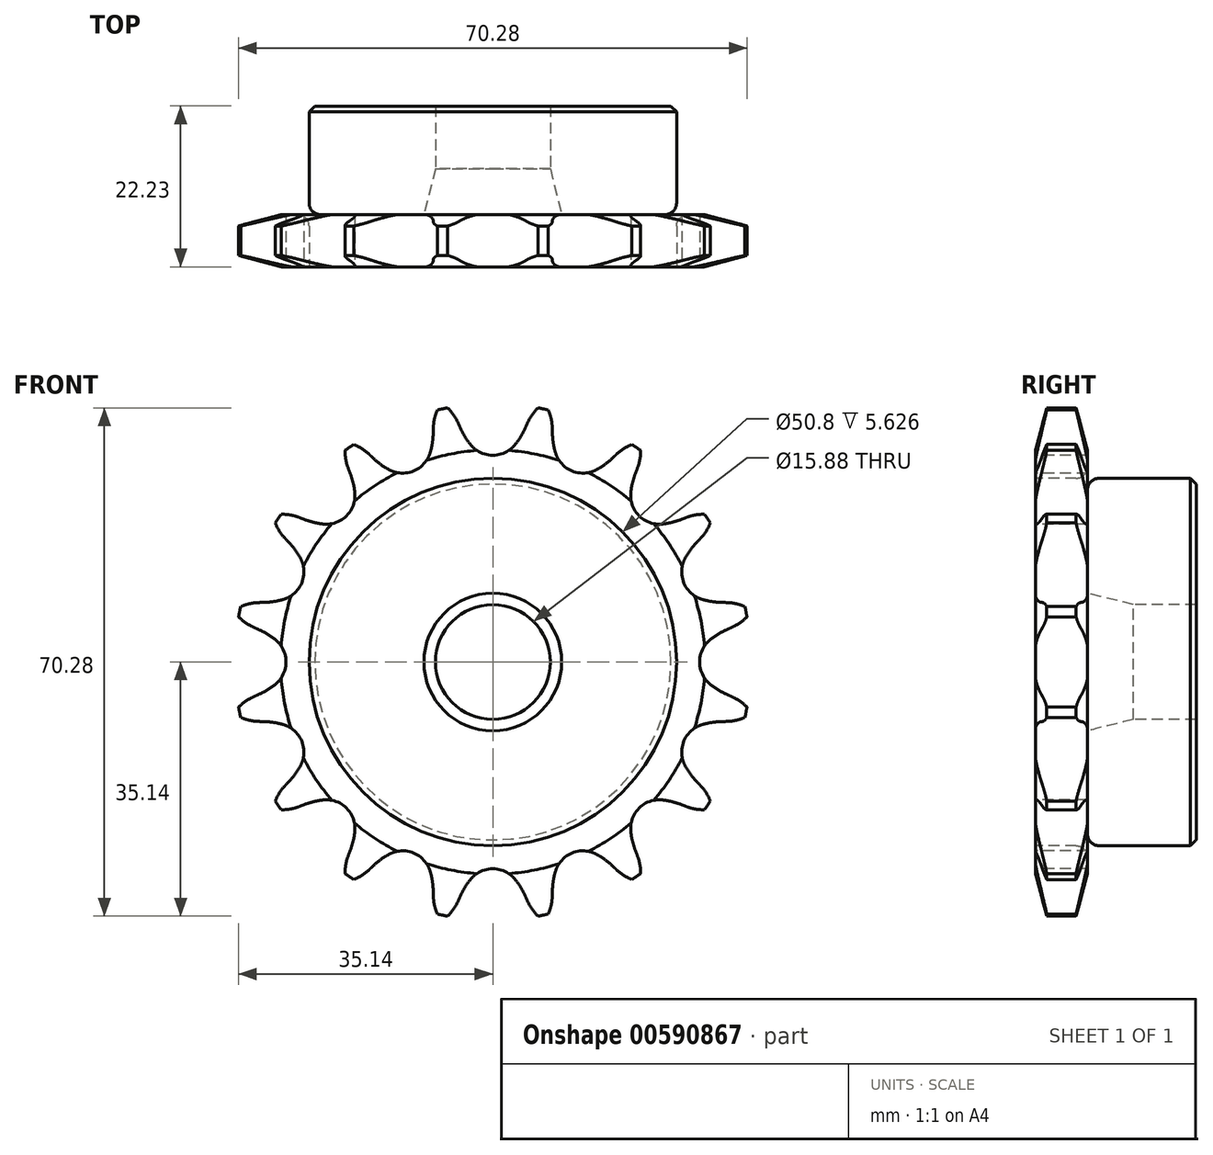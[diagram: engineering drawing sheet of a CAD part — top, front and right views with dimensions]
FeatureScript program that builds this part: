
annotation { "Feature Type Name" : "Feature", "Feature Type Description" : "" }
export const myFeature = defineFeature(function(context is Context, id is Id, definition is map)
    precondition{}
    {
        {
            var Q0;
            Q0=qCreatedBy(makeId("Right.planeOp"),FACE);
            var sketch = newSketch(context, id + "F0", { "sketchPlane" : qUnion([Q0])});
            skLineSegment(sketch, "E0", {"start": v(0, 0) * mm, "end": v(22.23, 0) * mm, "construction": true});
            skLineSegment(sketch, "E1.bottom", {"start": v(0, 7.94) * mm, "end": v(7.21, 7.94) * mm});
            skLineSegment(sketch, "E1.top", {"start": v(0, 35.69) * mm, "end": v(7.21, 35.69) * mm});
            skLineSegment(sketch, "E1.left", {"start": v(0, 7.94) * mm, "end": v(0, 35.69) * mm});
            skLineSegment(sketch, "E1.right", {"start": v(7.21, 7.94) * mm, "end": v(7.21, 35.69) * mm});
            skLineSegment(sketch, "E2.bottom", {"start": v(0, 7.94) * mm, "end": v(22.23, 7.94) * mm});
            skLineSegment(sketch, "E2.top", {"start": v(0, 25.4) * mm, "end": v(22.23, 25.4) * mm});
            skLineSegment(sketch, "E2.left", {"start": v(0, 7.94) * mm, "end": v(0, 25.4) * mm});
            skLineSegment(sketch, "E2.right", {"start": v(22.23, 7.94) * mm, "end": v(22.22, 25.4) * mm});
            skLineSegment(sketch, "E3.MirrorCS", {"start": v(0, -7.94) * mm, "end": v(7.21, -7.94) * mm});
            skLineSegment(sketch, "E4.MirrorCS", {"start": v(22.23, -7.94) * mm, "end": v(22.23, -25.4) * mm});
            skLineSegment(sketch, "E5.MirrorCS", {"start": v(0, -7.94) * mm, "end": v(0, -25.4) * mm});
            skLineSegment(sketch, "E6.MirrorCS", {"start": v(0, -35.69) * mm, "end": v(7.21, -35.69) * mm});
            skLineSegment(sketch, "E7.MirrorCS", {"start": v(0, -25.4) * mm, "end": v(22.23, -25.4) * mm});
            skLineSegment(sketch, "E8.MirrorCS", {"start": v(0, -7.94) * mm, "end": v(22.23, -7.94) * mm});
            skLineSegment(sketch, "E9.MirrorCS", {"start": v(0, -7.94) * mm, "end": v(0, -35.69) * mm});
            skLineSegment(sketch, "E10.MirrorCS", {"start": v(7.21, -7.94) * mm, "end": v(7.21, -35.69) * mm});
            skSolve(sketch);
        }
        {
            var Q0;
            {var subQ5=sQuery(id+"F0.wireOp",EDGE,"E2.right");Q0=makeQuery(id+"F0.imprint","IMPRINT",FACE,{"disambiguationData":[TD([[makeQuery(id+"F0.imprint","IMPRINT",EDGE,{"derivedFrom":subQ5}),1.0]])]});}
            var Q1;
            {var subQ5=sQuery(id+"F0.wireOp",EDGE,"E2.left");Q1=makeQuery(id+"F0.imprint","IMPRINT",FACE,{"disambiguationData":[TD([[makeQuery(id+"F0.imprint","IMPRINT",EDGE,{"derivedFrom":subQ5}),-1.0]])]});}
            var Q2;
            {var subQ0=sQuery(id+"F0.wireOp",EDGE,"E1.top");Q2=makeQuery(id+"F0.imprint","IMPRINT",FACE,{"disambiguationData":[TD([[makeQuery(id+"F0.imprint","IMPRINT",EDGE,{"derivedFrom":subQ0}),-1.0]])]});}
            var Q3;
            Q3=sQuery(id+"F0.wireOp",EDGE,"E0");
            revolve(context, id + "F1", {"entities" : qUnion([Q0, Q1, Q2]), "axis" : qUnion([Q3]), "revolveType" : RevolveType.FULL});
        }
        {
            var Q0;
            Q0=makeQuery(id+"F1.opRevolve","SWEPT_EDGE",EDGE,{"disambiguationData":[OSD([sQuery(id+"F0.wireOp",EDGE,"E1.right"),sQuery(id+"F0.wireOp",EDGE,"E2.top")])]});
            fillet(context, id + "F2", {"entities" : qUnion([Q0]), "radius" : 1.59 * mm, "tangentPropagation" : true, "allowEdgeOverflow" : false});
        }
        {
            var Q0;
            Q0=makeQuery(id+"F1.opRevolve","SWEPT_EDGE",EDGE,{"disambiguationData":[OSD([sQuery(id+"F0.wireOp",EDGE,"E2.top"),sQuery(id+"F0.wireOp",EDGE,"E2.right")])]});
            chamfer(context, id + "F3", {"entities" : qUnion([Q0]), "width" : 0.8 * mm, "tangentPropagation" : true});
        }
        {
            var Q0;
            Q0=makeQuery(id+"F1.opRevolve","SWEPT_EDGE",EDGE,{"disambiguationData":[OSD([sQuery(id+"F0.wireOp",EDGE,"E1.top"),sQuery(id+"F0.wireOp",EDGE,"E1.left")])]});
            var Q1;
            Q1=makeQuery(id+"F1.opRevolve","SWEPT_FACE",FACE,{"disambiguationData":[OSD([sQuery(id+"F0.wireOp",EDGE,"E1.right")])]});
            chamfer(context, id + "F4", {"entities" : qUnion([Q0, Q1]), "chamferType" : ChamferType.TWO_OFFSETS, "width1" : 6.35 * mm, "oppositeDirection" : false, "width2" : 1.57 * mm, "tangentPropagation" : true});
        }
        {
            var Q0;
            Q0=makeQuery(id+"F1.opRevolve","SWEPT_FACE",FACE,{"disambiguationData":[OSD([sQuery(id+"F0.wireOp",EDGE,"E1.left"),sQuery(id+"F0.wireOp",EDGE,"E2.left")])]});
            var sketch = newSketch(context, id + "F5", { "sketchPlane" : qUnion([Q0])});
            skCircle(sketch, "E11", {"center": v(0, 0) * mm, "radius": 32.55 * mm, "construction": true});
            skLineSegment(sketch, "E12", {"start": v(0, 0) * mm, "end": v(0, 32.55) * mm, "construction": true});
            skLineSegment(sketch, "E13", {"start": v(0, 32.55) * mm, "end": v(34.9, 32.55) * mm, "construction": true});
            skLineSegment(sketch, "E14", {"start": v(0, 32.55) * mm, "end": v(5, 36.56) * mm, "construction": true});
            skLineSegment(sketch, "E15", {"start": v(5, 36.56) * mm, "end": v(-4.46, 32.3) * mm, "construction": true});
            skLineSegment(sketch, "E16", {"start": v(-4.46, 32.3) * mm, "end": v(-4.82, 33.1) * mm});
            skLineSegment(sketch, "E17", {"start": v(0, 0) * mm, "end": v(-7.13, 35.85) * mm, "construction": true});
            skArc(sketch, "E18", {"start": v(-7.13, 35.85) * mm, "mid": v(-15.87, 26.15) * mm, "end": v(-4.82, 33.1) * mm, "construction": true});
            skLineSegment(sketch, "E19", {"start": v(-4.82, 33.1) * mm, "end": v(-4.82, 33.1) * mm});
            skArc(sketch, "E20", {"start": v(-4.82, 33.1) * mm, "mid": v(-5.78, 34.63) * mm, "end": v(-7.13, 35.85) * mm});
            skLineSegment(sketch, "E21", {"start": v(-4.46, 32.3) * mm, "end": v(-4.46, 32.3) * mm});
            skArc(sketch, "E22", {"start": v(-3.1, 30.07) * mm, "mid": v(13.83, 41.97) * mm, "end": v(-4.46, 32.3) * mm, "construction": true});
            skLineSegment(sketch, "E23", {"start": v(-4.82, 33.1) * mm, "end": v(-4.46, 32.3) * mm});
            skArc(sketch, "E24", {"start": v(-4.46, 32.3) * mm, "mid": v(-3.84, 31.14) * mm, "end": v(-3.1, 30.07) * mm});
            skArc(sketch, "E25.MirrorCS", {"start": v(4.82, 33.1) * mm, "mid": v(5.78, 34.63) * mm, "end": v(7.13, 35.85) * mm});
            skLineSegment(sketch, "E26.MirrorCS", {"start": v(4.82, 33.1) * mm, "end": v(4.46, 32.3) * mm});
            skArc(sketch, "E27.MirrorCS", {"start": v(4.46, 32.3) * mm, "mid": v(3.84, 31.14) * mm, "end": v(3.1, 30.07) * mm});
            skArc(sketch, "E28", {"start": v(3.1, 30.07) * mm, "mid": v(0, 36.51) * mm, "end": v(-3.1, 30.07) * mm, "construction": true});
            skArc(sketch, "E29", {"start": v(-3.1, 30.07) * mm, "mid": v(0, 28.59) * mm, "end": v(3.1, 30.07) * mm});
            skArc(sketch, "E30.1.0", {"start": v(-17.12, 28.74) * mm, "mid": v(-18.6, 29.79) * mm, "end": v(-20.3, 30.4) * mm});
            skLineSegment(sketch, "E30.1.1", {"start": v(-17.12, 28.74) * mm, "end": v(-16.48, 28.14) * mm});
            skArc(sketch, "E30.1.2", {"start": v(-16.48, 28.14) * mm, "mid": v(-15.47, 27.3) * mm, "end": v(-14.36, 26.6) * mm});
            skArc(sketch, "E30.1.3", {"start": v(-14.36, 26.6) * mm, "mid": v(-10.94, 26.41) * mm, "end": v(-8.65, 28.96) * mm});
            skArc(sketch, "E30.1.4", {"start": v(-8.24, 31.55) * mm, "mid": v(-8.37, 30.24) * mm, "end": v(-8.65, 28.96) * mm});
            skLineSegment(sketch, "E30.1.5", {"start": v(-8.22, 32.42) * mm, "end": v(-8.24, 31.55) * mm});
            skArc(sketch, "E30.1.6", {"start": v(-8.22, 32.42) * mm, "mid": v(-7.91, 34.21) * mm, "end": v(-7.13, 35.85) * mm});
            skArc(sketch, "E30.2.0", {"start": v(-26.8, 20) * mm, "mid": v(-28.58, 20.4) * mm, "end": v(-30.4, 20.3) * mm});
            skLineSegment(sketch, "E30.2.1", {"start": v(-26.8, 20) * mm, "end": v(-26, 19.69) * mm});
            skArc(sketch, "E30.2.2", {"start": v(-26, 19.69) * mm, "mid": v(-24.74, 19.3) * mm, "end": v(-23.45, 19.08) * mm});
            skArc(sketch, "E30.2.3", {"start": v(-23.45, 19.08) * mm, "mid": v(-20.21, 20.21) * mm, "end": v(-19.08, 23.45) * mm});
            skArc(sketch, "E30.2.4", {"start": v(-19.69, 26) * mm, "mid": v(-19.3, 24.74) * mm, "end": v(-19.08, 23.45) * mm});
            skLineSegment(sketch, "E30.2.5", {"start": v(-20, 26.8) * mm, "end": v(-19.69, 26) * mm});
            skArc(sketch, "E30.2.6", {"start": v(-20, 26.8) * mm, "mid": v(-20.4, 28.58) * mm, "end": v(-20.3, 30.4) * mm});
            skArc(sketch, "E30.3.0", {"start": v(-32.42, 8.22) * mm, "mid": v(-34.21, 7.91) * mm, "end": v(-35.85, 7.13) * mm});
            skLineSegment(sketch, "E30.3.1", {"start": v(-32.42, 8.22) * mm, "end": v(-31.55, 8.24) * mm});
            skArc(sketch, "E30.3.2", {"start": v(-31.55, 8.24) * mm, "mid": v(-30.24, 8.37) * mm, "end": v(-28.96, 8.65) * mm});
            skArc(sketch, "E30.3.3", {"start": v(-28.96, 8.65) * mm, "mid": v(-26.41, 10.94) * mm, "end": v(-26.6, 14.36) * mm});
            skArc(sketch, "E30.3.4", {"start": v(-28.14, 16.48) * mm, "mid": v(-27.3, 15.47) * mm, "end": v(-26.6, 14.36) * mm});
            skLineSegment(sketch, "E30.3.5", {"start": v(-28.74, 17.12) * mm, "end": v(-28.14, 16.48) * mm});
            skArc(sketch, "E30.3.6", {"start": v(-28.74, 17.12) * mm, "mid": v(-29.79, 18.6) * mm, "end": v(-30.4, 20.3) * mm});
            skArc(sketch, "E30.4.0", {"start": v(-33.1, -4.82) * mm, "mid": v(-34.63, -5.78) * mm, "end": v(-35.85, -7.13) * mm});
            skLineSegment(sketch, "E30.4.1", {"start": v(-33.1, -4.82) * mm, "end": v(-32.3, -4.46) * mm});
            skArc(sketch, "E30.4.2", {"start": v(-32.3, -4.46) * mm, "mid": v(-31.14, -3.84) * mm, "end": v(-30.07, -3.1) * mm});
            skArc(sketch, "E30.4.3", {"start": v(-30.07, -3.1) * mm, "mid": v(-28.59, 0) * mm, "end": v(-30.07, 3.1) * mm});
            skArc(sketch, "E30.4.4", {"start": v(-32.3, 4.46) * mm, "mid": v(-31.14, 3.84) * mm, "end": v(-30.07, 3.1) * mm});
            skLineSegment(sketch, "E30.4.5", {"start": v(-33.1, 4.82) * mm, "end": v(-32.3, 4.46) * mm});
            skArc(sketch, "E30.4.6", {"start": v(-33.1, 4.82) * mm, "mid": v(-34.63, 5.78) * mm, "end": v(-35.85, 7.13) * mm});
            skArc(sketch, "E30.5.0", {"start": v(-28.74, -17.12) * mm, "mid": v(-29.79, -18.6) * mm, "end": v(-30.4, -20.3) * mm});
            skLineSegment(sketch, "E30.5.1", {"start": v(-28.74, -17.12) * mm, "end": v(-28.14, -16.48) * mm});
            skArc(sketch, "E30.5.2", {"start": v(-28.14, -16.48) * mm, "mid": v(-27.3, -15.47) * mm, "end": v(-26.6, -14.36) * mm});
            skArc(sketch, "E30.5.3", {"start": v(-26.6, -14.36) * mm, "mid": v(-26.41, -10.94) * mm, "end": v(-28.96, -8.65) * mm});
            skArc(sketch, "E30.5.4", {"start": v(-31.55, -8.24) * mm, "mid": v(-30.24, -8.37) * mm, "end": v(-28.96, -8.65) * mm});
            skLineSegment(sketch, "E30.5.5", {"start": v(-32.42, -8.22) * mm, "end": v(-31.55, -8.24) * mm});
            skArc(sketch, "E30.5.6", {"start": v(-32.42, -8.22) * mm, "mid": v(-34.21, -7.91) * mm, "end": v(-35.85, -7.13) * mm});
            skArc(sketch, "E30.6.0", {"start": v(-20, -26.8) * mm, "mid": v(-20.4, -28.58) * mm, "end": v(-20.3, -30.4) * mm});
            skLineSegment(sketch, "E30.6.1", {"start": v(-20, -26.8) * mm, "end": v(-19.69, -26) * mm});
            skArc(sketch, "E30.6.2", {"start": v(-19.69, -26) * mm, "mid": v(-19.3, -24.74) * mm, "end": v(-19.08, -23.45) * mm});
            skArc(sketch, "E30.6.3", {"start": v(-19.08, -23.45) * mm, "mid": v(-20.21, -20.21) * mm, "end": v(-23.45, -19.08) * mm});
            skArc(sketch, "E30.6.4", {"start": v(-26, -19.69) * mm, "mid": v(-24.74, -19.3) * mm, "end": v(-23.45, -19.08) * mm});
            skLineSegment(sketch, "E30.6.5", {"start": v(-26.8, -20) * mm, "end": v(-26, -19.69) * mm});
            skArc(sketch, "E30.6.6", {"start": v(-26.8, -20) * mm, "mid": v(-28.58, -20.4) * mm, "end": v(-30.4, -20.3) * mm});
            skArc(sketch, "E30.7.0", {"start": v(-8.22, -32.42) * mm, "mid": v(-7.91, -34.21) * mm, "end": v(-7.13, -35.85) * mm});
            skLineSegment(sketch, "E30.7.1", {"start": v(-8.22, -32.42) * mm, "end": v(-8.24, -31.55) * mm});
            skArc(sketch, "E30.7.2", {"start": v(-8.24, -31.55) * mm, "mid": v(-8.37, -30.24) * mm, "end": v(-8.65, -28.96) * mm});
            skArc(sketch, "E30.7.3", {"start": v(-8.65, -28.96) * mm, "mid": v(-10.94, -26.41) * mm, "end": v(-14.36, -26.6) * mm});
            skArc(sketch, "E30.7.4", {"start": v(-16.48, -28.14) * mm, "mid": v(-15.47, -27.3) * mm, "end": v(-14.36, -26.6) * mm});
            skLineSegment(sketch, "E30.7.5", {"start": v(-17.12, -28.74) * mm, "end": v(-16.48, -28.14) * mm});
            skArc(sketch, "E30.7.6", {"start": v(-17.12, -28.74) * mm, "mid": v(-18.6, -29.79) * mm, "end": v(-20.3, -30.4) * mm});
            skArc(sketch, "E30.8.0", {"start": v(4.82, -33.1) * mm, "mid": v(5.78, -34.63) * mm, "end": v(7.13, -35.85) * mm});
            skLineSegment(sketch, "E30.8.1", {"start": v(4.82, -33.1) * mm, "end": v(4.46, -32.3) * mm});
            skArc(sketch, "E30.8.2", {"start": v(4.46, -32.3) * mm, "mid": v(3.84, -31.14) * mm, "end": v(3.1, -30.07) * mm});
            skArc(sketch, "E30.8.3", {"start": v(3.1, -30.07) * mm, "mid": v(0, -28.59) * mm, "end": v(-3.1, -30.07) * mm});
            skArc(sketch, "E30.8.4", {"start": v(-4.46, -32.3) * mm, "mid": v(-3.84, -31.14) * mm, "end": v(-3.1, -30.07) * mm});
            skLineSegment(sketch, "E30.8.5", {"start": v(-4.82, -33.1) * mm, "end": v(-4.46, -32.3) * mm});
            skArc(sketch, "E30.8.6", {"start": v(-4.82, -33.1) * mm, "mid": v(-5.78, -34.63) * mm, "end": v(-7.13, -35.85) * mm});
            skArc(sketch, "E30.9.0", {"start": v(17.12, -28.74) * mm, "mid": v(18.6, -29.79) * mm, "end": v(20.3, -30.4) * mm});
            skLineSegment(sketch, "E30.9.1", {"start": v(17.12, -28.74) * mm, "end": v(16.48, -28.14) * mm});
            skArc(sketch, "E30.9.2", {"start": v(16.48, -28.14) * mm, "mid": v(15.47, -27.3) * mm, "end": v(14.36, -26.6) * mm});
            skArc(sketch, "E30.9.3", {"start": v(14.36, -26.6) * mm, "mid": v(10.94, -26.41) * mm, "end": v(8.65, -28.96) * mm});
            skArc(sketch, "E30.9.4", {"start": v(8.24, -31.55) * mm, "mid": v(8.37, -30.24) * mm, "end": v(8.65, -28.96) * mm});
            skLineSegment(sketch, "E30.9.5", {"start": v(8.22, -32.42) * mm, "end": v(8.24, -31.55) * mm});
            skArc(sketch, "E30.9.6", {"start": v(8.22, -32.42) * mm, "mid": v(7.91, -34.21) * mm, "end": v(7.13, -35.85) * mm});
            skArc(sketch, "E30.10.0", {"start": v(26.8, -20) * mm, "mid": v(28.58, -20.4) * mm, "end": v(30.4, -20.3) * mm});
            skLineSegment(sketch, "E30.10.1", {"start": v(26.8, -20) * mm, "end": v(26, -19.69) * mm});
            skArc(sketch, "E30.10.2", {"start": v(26, -19.69) * mm, "mid": v(24.74, -19.3) * mm, "end": v(23.45, -19.08) * mm});
            skArc(sketch, "E30.10.3", {"start": v(23.45, -19.08) * mm, "mid": v(20.21, -20.21) * mm, "end": v(19.08, -23.45) * mm});
            skArc(sketch, "E30.10.4", {"start": v(19.69, -26) * mm, "mid": v(19.3, -24.74) * mm, "end": v(19.08, -23.45) * mm});
            skLineSegment(sketch, "E30.10.5", {"start": v(20, -26.8) * mm, "end": v(19.69, -26) * mm});
            skArc(sketch, "E30.10.6", {"start": v(20, -26.8) * mm, "mid": v(20.4, -28.58) * mm, "end": v(20.3, -30.4) * mm});
            skArc(sketch, "E30.11.0", {"start": v(32.42, -8.22) * mm, "mid": v(34.21, -7.91) * mm, "end": v(35.85, -7.13) * mm});
            skLineSegment(sketch, "E30.11.1", {"start": v(32.42, -8.22) * mm, "end": v(31.55, -8.24) * mm});
            skArc(sketch, "E30.11.2", {"start": v(31.55, -8.24) * mm, "mid": v(30.24, -8.37) * mm, "end": v(28.96, -8.65) * mm});
            skArc(sketch, "E30.11.3", {"start": v(28.96, -8.65) * mm, "mid": v(26.41, -10.94) * mm, "end": v(26.6, -14.36) * mm});
            skArc(sketch, "E30.11.4", {"start": v(28.14, -16.48) * mm, "mid": v(27.3, -15.47) * mm, "end": v(26.6, -14.36) * mm});
            skLineSegment(sketch, "E30.11.5", {"start": v(28.74, -17.12) * mm, "end": v(28.14, -16.48) * mm});
            skArc(sketch, "E30.11.6", {"start": v(28.74, -17.12) * mm, "mid": v(29.79, -18.6) * mm, "end": v(30.4, -20.3) * mm});
            skArc(sketch, "E30.12.0", {"start": v(33.1, 4.82) * mm, "mid": v(34.63, 5.78) * mm, "end": v(35.85, 7.13) * mm});
            skLineSegment(sketch, "E30.12.1", {"start": v(33.1, 4.82) * mm, "end": v(32.3, 4.46) * mm});
            skArc(sketch, "E30.12.2", {"start": v(32.3, 4.46) * mm, "mid": v(31.14, 3.84) * mm, "end": v(30.07, 3.1) * mm});
            skArc(sketch, "E30.12.3", {"start": v(30.07, 3.1) * mm, "mid": v(28.59, 0) * mm, "end": v(30.07, -3.1) * mm});
            skArc(sketch, "E30.12.4", {"start": v(32.3, -4.46) * mm, "mid": v(31.14, -3.84) * mm, "end": v(30.07, -3.1) * mm});
            skLineSegment(sketch, "E30.12.5", {"start": v(33.1, -4.82) * mm, "end": v(32.3, -4.46) * mm});
            skArc(sketch, "E30.12.6", {"start": v(33.1, -4.82) * mm, "mid": v(34.63, -5.78) * mm, "end": v(35.85, -7.13) * mm});
            skArc(sketch, "E30.13.0", {"start": v(28.74, 17.12) * mm, "mid": v(29.79, 18.6) * mm, "end": v(30.4, 20.3) * mm});
            skLineSegment(sketch, "E30.13.1", {"start": v(28.74, 17.12) * mm, "end": v(28.14, 16.48) * mm});
            skArc(sketch, "E30.13.2", {"start": v(28.14, 16.48) * mm, "mid": v(27.3, 15.47) * mm, "end": v(26.6, 14.36) * mm});
            skArc(sketch, "E30.13.3", {"start": v(26.6, 14.36) * mm, "mid": v(26.41, 10.94) * mm, "end": v(28.96, 8.65) * mm});
            skArc(sketch, "E30.13.4", {"start": v(31.55, 8.24) * mm, "mid": v(30.24, 8.37) * mm, "end": v(28.96, 8.65) * mm});
            skLineSegment(sketch, "E30.13.5", {"start": v(32.42, 8.22) * mm, "end": v(31.55, 8.24) * mm});
            skArc(sketch, "E30.13.6", {"start": v(32.42, 8.22) * mm, "mid": v(34.21, 7.91) * mm, "end": v(35.85, 7.13) * mm});
            skArc(sketch, "E30.14.0", {"start": v(20, 26.8) * mm, "mid": v(20.4, 28.58) * mm, "end": v(20.3, 30.4) * mm});
            skLineSegment(sketch, "E30.14.1", {"start": v(20, 26.8) * mm, "end": v(19.69, 26) * mm});
            skArc(sketch, "E30.14.2", {"start": v(19.69, 26) * mm, "mid": v(19.3, 24.74) * mm, "end": v(19.08, 23.45) * mm});
            skArc(sketch, "E30.14.3", {"start": v(19.08, 23.45) * mm, "mid": v(20.21, 20.21) * mm, "end": v(23.45, 19.08) * mm});
            skArc(sketch, "E30.14.4", {"start": v(26, 19.69) * mm, "mid": v(24.74, 19.3) * mm, "end": v(23.45, 19.08) * mm});
            skLineSegment(sketch, "E30.14.5", {"start": v(26.8, 20) * mm, "end": v(26, 19.69) * mm});
            skArc(sketch, "E30.14.6", {"start": v(26.8, 20) * mm, "mid": v(28.58, 20.4) * mm, "end": v(30.4, 20.3) * mm});
            skArc(sketch, "E30.15.0", {"start": v(8.22, 32.42) * mm, "mid": v(7.91, 34.21) * mm, "end": v(7.13, 35.85) * mm});
            skLineSegment(sketch, "E30.15.1", {"start": v(8.22, 32.42) * mm, "end": v(8.24, 31.55) * mm});
            skArc(sketch, "E30.15.2", {"start": v(8.24, 31.55) * mm, "mid": v(8.37, 30.24) * mm, "end": v(8.65, 28.96) * mm});
            skArc(sketch, "E30.15.3", {"start": v(8.65, 28.96) * mm, "mid": v(10.94, 26.41) * mm, "end": v(14.36, 26.6) * mm});
            skArc(sketch, "E30.15.4", {"start": v(16.48, 28.14) * mm, "mid": v(15.47, 27.3) * mm, "end": v(14.36, 26.6) * mm});
            skLineSegment(sketch, "E30.15.5", {"start": v(17.12, 28.74) * mm, "end": v(16.48, 28.14) * mm});
            skArc(sketch, "E30.15.6", {"start": v(17.12, 28.74) * mm, "mid": v(18.6, 29.79) * mm, "end": v(20.3, 30.4) * mm});
            skSolve(sketch);
        }
        {
            var Q0;
            Q0 = qSketchRegion(id + "F5", true);
            extrude(context, id + "F6", {"entities" : qUnion([Q0]), "operationType" : NewBodyOperationType.INTERSECT, "endBound" : BoundingType.THROUGH_ALL, "oppositeDirection" : true, "depth" : 25.4 * mm, "offsetDistance" : 25.4 * mm});
        }
    });
